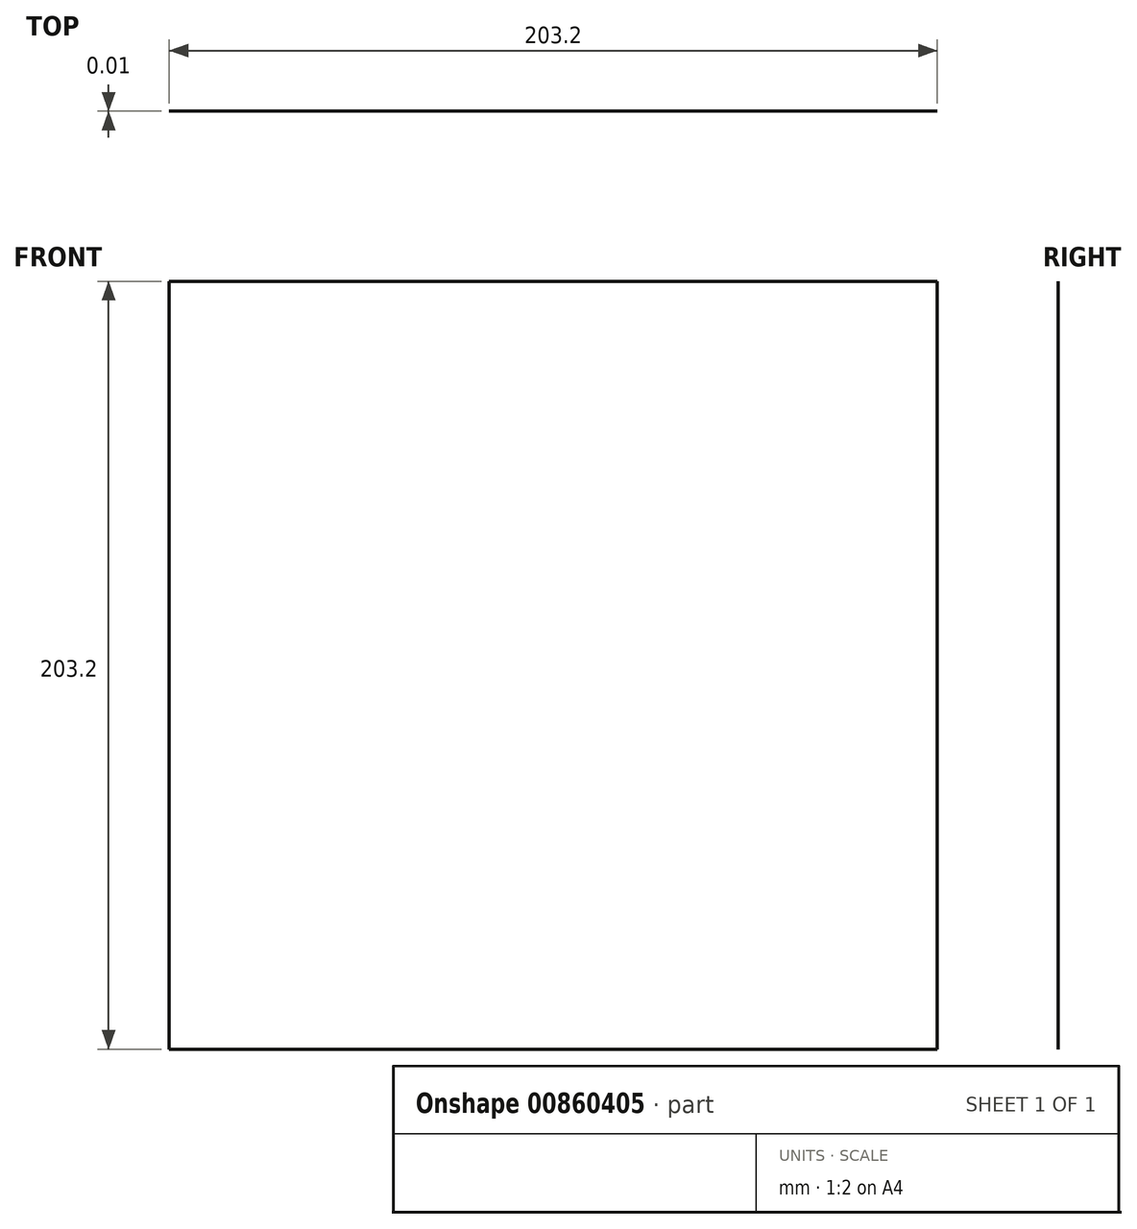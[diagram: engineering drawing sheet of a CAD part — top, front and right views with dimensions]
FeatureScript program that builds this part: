
annotation { "Feature Type Name" : "Feature", "Feature Type Description" : "" }
export const myFeature = defineFeature(function(context is Context, id is Id, definition is map)
    precondition{}
    {
        {
            var Q0;
            Q0=qCreatedBy(makeId("Front.planeOp"),FACE);
            var sketch = newSketch(context, id + "F0", { "sketchPlane" : qUnion([Q0])});
            skLineSegment(sketch, "E0.bottom", {"start": v(0, 0) * mm, "end": v(203.2, 0) * mm});
            skLineSegment(sketch, "E0.top", {"start": v(0, 203.2) * mm, "end": v(203.2, 203.2) * mm});
            skLineSegment(sketch, "E0.left", {"start": v(0, 0) * mm, "end": v(0, 203.2) * mm});
            skLineSegment(sketch, "E0.right", {"start": v(203.2, 0) * mm, "end": v(203.2, 203.2) * mm});
            skSolve(sketch);
        }
        {
            var Q0;
            Q0 = qSketchRegion(id + "F0", true);
            extrude(context, id + "F1", {"entities" : qUnion([Q0]), "depth" : 1 / 101.6 * mm, "offsetDistance" : 25.4 * mm});
        }
    });
